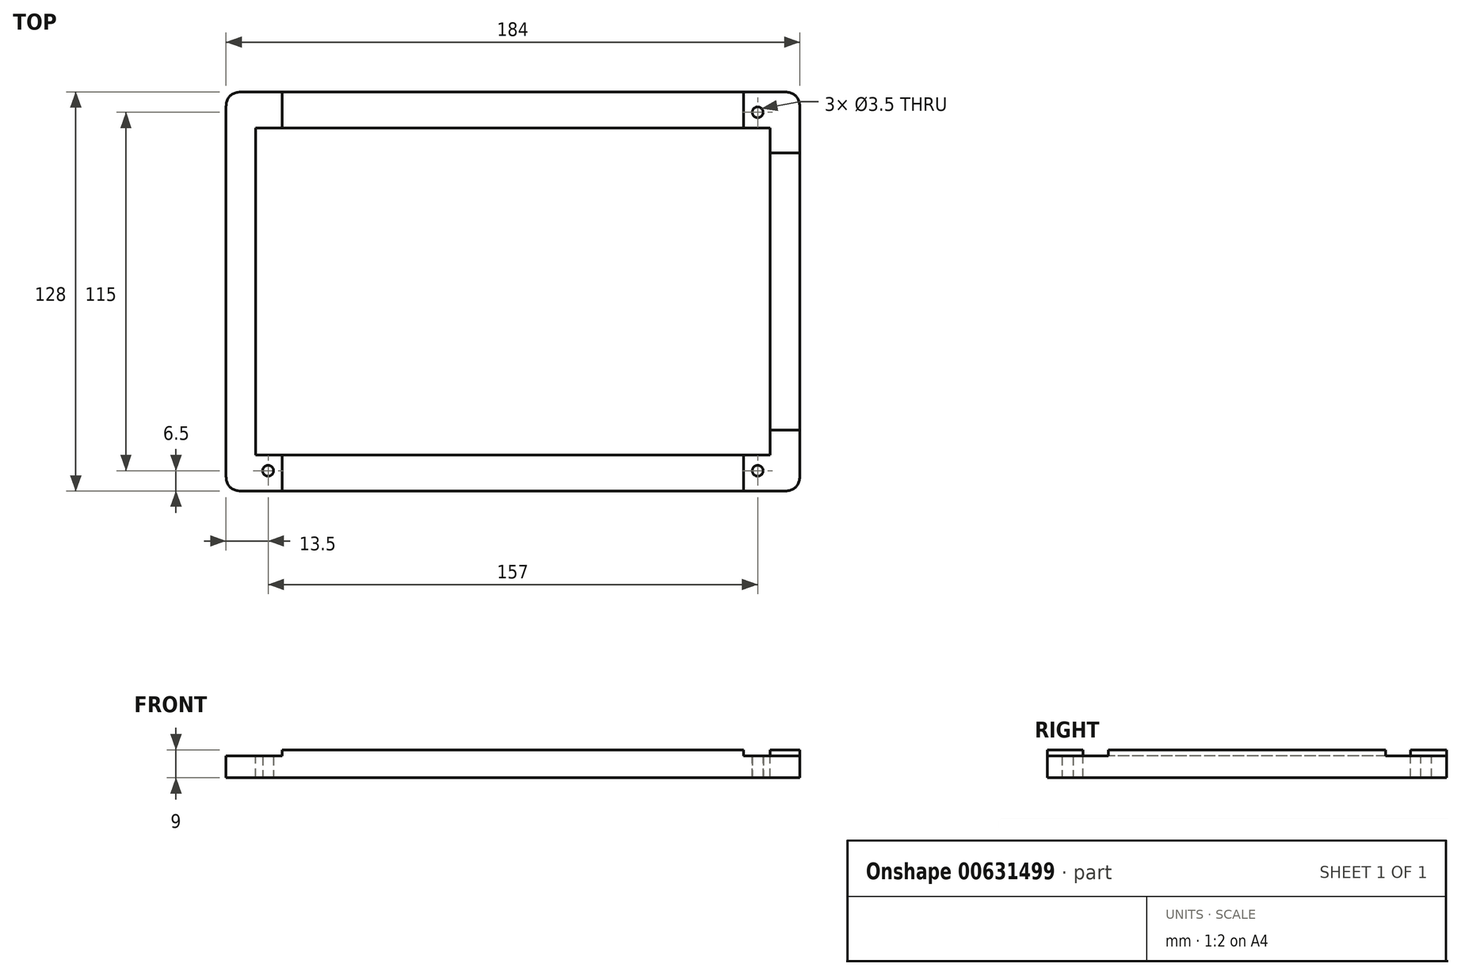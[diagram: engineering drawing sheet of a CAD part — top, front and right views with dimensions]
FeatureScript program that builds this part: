
annotation { "Feature Type Name" : "Feature", "Feature Type Description" : "" }
export const myFeature = defineFeature(function(context is Context, id is Id, definition is map)
    precondition{}
    {
        {
            var Q0;
            Q0=qCreatedBy(makeId("Top.planeOp"),FACE);
            var sketch = newSketch(context, id + "F0", { "sketchPlane" : qUnion([Q0])});
            skLineSegment(sketch, "E0.bottom", {"start": v(92, 64) * mm, "end": v(-92, 64) * mm});
            skLineSegment(sketch, "E0.top", {"start": v(92, -64) * mm, "end": v(-92, -64) * mm});
            skLineSegment(sketch, "E0.left", {"start": v(92, 64) * mm, "end": v(92, -64) * mm});
            skLineSegment(sketch, "E0.right", {"start": v(-92, 64) * mm, "end": v(-92, -64) * mm});
            skPoint(sketch, "E0.middle", {"position": v(0, 0) * mm});
            skSolve(sketch);
        }
        {
            var Q0;
            Q0=makeQuery(id+"F0.imprint","IMPRINT",FACE,{"disambiguationData":[TD([[makeQuery(id+"F0.imprint","IMPRINT",EDGE,{"derivedFrom":sQuery(id+"F0.wireOp",EDGE,"E0.bottom")}),1.0]])]});
            extrude(context, id + "F1", {"entities" : qUnion([Q0]), "depth" : 7 * mm, "offsetDistance" : 25.4 * mm});
        }
        {
            var Q0;
            Q0=makeQuery(id+"F1.opExtrude","CAP_FACE",FACE,{"disambiguationData":[OSD([sQuery(id+"F0.wireOp",EDGE,"E0.bottom"),sQuery(id+"F0.wireOp",EDGE,"E0.top"),sQuery(id+"F0.wireOp",EDGE,"E0.left"),sQuery(id+"F0.wireOp",EDGE,"E0.right")])],"isStart":false});
            var sketch = newSketch(context, id + "F2", { "sketchPlane" : qUnion([Q0])});
            skLineSegment(sketch, "E1.bottom", {"start": v(82.5, 52.5) * mm, "end": v(-82.5, 52.5) * mm});
            skLineSegment(sketch, "E1.top", {"start": v(82.5, -52.5) * mm, "end": v(-82.5, -52.5) * mm});
            skLineSegment(sketch, "E1.left", {"start": v(82.5, 52.5) * mm, "end": v(82.5, -52.5) * mm});
            skLineSegment(sketch, "E1.right", {"start": v(-82.5, 52.5) * mm, "end": v(-82.5, -52.5) * mm});
            skPoint(sketch, "E1.middle", {"position": v(0, 0) * mm});
            skSolve(sketch);
        }
        {
            var Q0;
            Q0=makeQuery(id+"F2.imprint","IMPRINT",FACE,{"disambiguationData":[TD([[makeQuery(id+"F2.imprint","IMPRINT",EDGE,{"derivedFrom":sQuery(id+"F2.wireOp",EDGE,"E1.bottom")}),1.0]])]});
            var Q1;
            Q1=makeQuery(id+"F1.opExtrude","CAP_FACE",FACE,{"disambiguationData":[OSD([sQuery(id+"F0.wireOp",EDGE,"E0.bottom"),sQuery(id+"F0.wireOp",EDGE,"E0.top"),sQuery(id+"F0.wireOp",EDGE,"E0.left"),sQuery(id+"F0.wireOp",EDGE,"E0.right")])],"isStart":true});
            extrude(context, id + "F3", {"entities" : qUnion([Q0]), "operationType" : NewBodyOperationType.REMOVE, "endBound" : BoundingType.UP_TO_SURFACE, "oppositeDirection" : true, "depth" : 25.4 * mm, "endBoundEntityFace" : qUnion([Q1]), "offsetDistance" : 25.4 * mm});
        }
        {
            var Q0;
            Q0=makeQuery(id+"F1.opExtrude","CAP_FACE",FACE,{"disambiguationData":[OSD([sQuery(id+"F0.wireOp",EDGE,"E0.bottom"),sQuery(id+"F0.wireOp",EDGE,"E0.top"),sQuery(id+"F0.wireOp",EDGE,"E0.left"),sQuery(id+"F0.wireOp",EDGE,"E0.right")])],"isStart":false});
            var sketch = newSketch(context, id + "F4", { "sketchPlane" : qUnion([Q0])});
            skLineSegment(sketch, "E2", {"start": v(0, 64) * mm, "end": v(0, 52.5) * mm});
            skLineSegment(sketch, "E3.bottom", {"start": v(74, 64) * mm, "end": v(-74, 64) * mm});
            skLineSegment(sketch, "E3.top", {"start": v(74, 52.5) * mm, "end": v(-74, 52.5) * mm});
            skLineSegment(sketch, "E3.left", {"start": v(74, 64) * mm, "end": v(74, 52.5) * mm});
            skLineSegment(sketch, "E3.right", {"start": v(-74, 64) * mm, "end": v(-74, 52.5) * mm});
            skPoint(sketch, "E3.middle", {"position": v(0, 58.25) * mm});
            skLineSegment(sketch, "E4", {"start": v(0, -52.5) * mm, "end": v(0, -64) * mm});
            skLineSegment(sketch, "E5.bottom", {"start": v(74, -52.5) * mm, "end": v(-74, -52.5) * mm});
            skLineSegment(sketch, "E5.top", {"start": v(74, -64) * mm, "end": v(-74, -64) * mm});
            skLineSegment(sketch, "E5.left", {"start": v(74, -52.5) * mm, "end": v(74, -64) * mm});
            skLineSegment(sketch, "E5.right", {"start": v(-74, -52.5) * mm, "end": v(-74, -64) * mm});
            skPoint(sketch, "E5.middle", {"position": v(0, -58.25) * mm});
            skSolve(sketch);
        }
        {
            var Q0;
            {var subQ0=sQuery(id+"F4.wireOp",EDGE,"E2");Q0=makeQuery(id+"F4.imprint","IMPRINT",FACE,{"disambiguationData":[TD([[makeQuery(id+"F4.imprint","IMPRINT",EDGE,{"derivedFrom":subQ0}),-1.0]])]});}
            var Q1;
            {var subQ0=sQuery(id+"F4.wireOp",EDGE,"E2");Q1=makeQuery(id+"F4.imprint","IMPRINT",FACE,{"disambiguationData":[TD([[makeQuery(id+"F4.imprint","IMPRINT",EDGE,{"derivedFrom":subQ0}),1.0]])]});}
            var Q2;
            {var subQ0=sQuery(id+"F4.wireOp",EDGE,"E4");Q2=makeQuery(id+"F4.imprint","IMPRINT",FACE,{"disambiguationData":[TD([[makeQuery(id+"F4.imprint","IMPRINT",EDGE,{"derivedFrom":subQ0}),-1.0]])]});}
            var Q3;
            {var subQ0=sQuery(id+"F4.wireOp",EDGE,"E4");Q3=makeQuery(id+"F4.imprint","IMPRINT",FACE,{"disambiguationData":[TD([[makeQuery(id+"F4.imprint","IMPRINT",EDGE,{"derivedFrom":subQ0}),1.0]])]});}
            extrude(context, id + "F5", {"entities" : qUnion([Q0, Q1, Q2, Q3]), "operationType" : NewBodyOperationType.ADD, "depth" : 2 * mm, "offsetDistance" : 25.4 * mm});
        }
        {
            var Q0;
            Q0=makeQuery(id+"F1.opExtrude","SWEPT_EDGE",EDGE,{"disambiguationData":[OSD([sQuery(id+"F0.wireOp",EDGE,"E0.top"),sQuery(id+"F0.wireOp",EDGE,"E0.left")])]});
            var Q1;
            Q1=makeQuery(id+"F1.opExtrude","SWEPT_EDGE",EDGE,{"disambiguationData":[OSD([sQuery(id+"F0.wireOp",EDGE,"E0.bottom"),sQuery(id+"F0.wireOp",EDGE,"E0.left")])]});
            var Q2;
            Q2=makeQuery(id+"F1.opExtrude","SWEPT_EDGE",EDGE,{"disambiguationData":[OSD([sQuery(id+"F0.wireOp",EDGE,"E0.bottom"),sQuery(id+"F0.wireOp",EDGE,"E0.right")])]});
            var Q3;
            Q3=makeQuery(id+"F1.opExtrude","SWEPT_EDGE",EDGE,{"disambiguationData":[OSD([sQuery(id+"F0.wireOp",EDGE,"E0.top"),sQuery(id+"F0.wireOp",EDGE,"E0.right")])]});
            fillet(context, id + "F6", {"entities" : qUnion([Q0, Q1, Q2, Q3]), "radius" : 5.08 * mm, "tangentPropagation" : true, "rho" : 0.5, "crossSection" : FilletCrossSection.CONIC, "allowEdgeOverflow" : false});
        }
        {
            var Q0;
            {var subQ0=sQuery(id+"F0.wireOp",EDGE,"E0.bottom");var subQ1=sQuery(id+"F0.wireOp",EDGE,"E0.top");var subQ2=sQuery(id+"F0.wireOp",EDGE,"E0.left");Q0=makeQuery(id+"F5.boolean.opBoolean","SPLIT",FACE,{"disambiguationData":[TD([makeQuery(id+"F1.opExtrude","SWEPT_FACE",FACE,{"disambiguationData":[OSD([subQ2])]})])],"derivedFrom":makeQuery(id+"F1.opExtrude","CAP_FACE",FACE,{"disambiguationData":[OSD([subQ0,subQ1,subQ2,sQuery(id+"F0.wireOp",EDGE,"E0.right")])],"isStart":false})});}
            var sketch = newSketch(context, id + "F7", { "sketchPlane" : qUnion([Q0])});
            skLineSegment(sketch, "E6", {"start": v(92, 0) * mm, "end": v(82.5, 0) * mm});
            skLineSegment(sketch, "E7.bottom", {"start": v(92, -44.45) * mm, "end": v(82.5, -44.45) * mm});
            skLineSegment(sketch, "E7.top", {"start": v(92, 44.45) * mm, "end": v(82.5, 44.45) * mm});
            skLineSegment(sketch, "E7.left", {"start": v(92, -44.45) * mm, "end": v(92, 44.45) * mm});
            skLineSegment(sketch, "E7.right", {"start": v(82.5, -44.45) * mm, "end": v(82.5, 44.45) * mm});
            skPoint(sketch, "E7.middle", {"position": v(87.25, 0) * mm});
            skSolve(sketch);
        }
        {
            var Q0;
            {var subQ0=sQuery(id+"F7.wireOp",EDGE,"E6");Q0=makeQuery(id+"F7.imprint","IMPRINT",FACE,{"disambiguationData":[TD([[makeQuery(id+"F7.imprint","IMPRINT",EDGE,{"derivedFrom":subQ0}),1.0]])]});}
            var Q1;
            {var subQ0=sQuery(id+"F7.wireOp",EDGE,"E6");Q1=makeQuery(id+"F7.imprint","IMPRINT",FACE,{"disambiguationData":[TD([[makeQuery(id+"F7.imprint","IMPRINT",EDGE,{"derivedFrom":subQ0}),-1.0]])]});}
            extrude(context, id + "F8", {"entities" : qUnion([Q0, Q1]), "operationType" : NewBodyOperationType.ADD, "depth" : 2 * mm, "offsetDistance" : 25.4 * mm});
        }
        {
            var Q0;
            {var subQ1=sQuery(id+"F0.wireOp",EDGE,"E0.left");var subQ2=sQuery(id+"F0.wireOp",EDGE,"E0.bottom");var subQ5=makeQuery(id+"F1.opExtrude","SWEPT_FACE",FACE,{"disambiguationData":[OSD([subQ2])]});var subQ6=makeQuery(id+"F1.opExtrude","SWEPT_FACE",FACE,{"disambiguationData":[OSD([subQ1])]});var subQ9=sQuery(id+"F0.wireOp",EDGE,"E0.top");Q0=makeQuery(id+"F8.boolean.opBoolean","SPLIT",FACE,{"disambiguationData":[TD([subQ5])],"derivedFrom":makeQuery(id+"F5.boolean.opBoolean","SPLIT",FACE,{"disambiguationData":[TD([subQ6])],"derivedFrom":makeQuery(id+"F1.opExtrude","CAP_FACE",FACE,{"disambiguationData":[OSD([subQ2,subQ9,subQ1,sQuery(id+"F0.wireOp",EDGE,"E0.right")])],"isStart":false})})});}
            var sketch = newSketch(context, id + "F9", { "sketchPlane" : qUnion([Q0])});
            skLineSegment(sketch, "E8", {"start": v(82.5, 49.76) * mm, "end": v(78.5, 49.76) * mm});
            skLineSegment(sketch, "E9", {"start": v(78.5, 49.76) * mm, "end": v(78.5, 57.5) * mm});
            skCircle(sketch, "E10", {"center": v(78.5, 57.5) * mm, "radius": 1.75 * mm});
            skSolve(sketch);
        }
        {
            var Q0;
            Q0=makeQuery(id+"F9.imprint","IMPRINT",FACE,{"disambiguationData":[TD([[makeQuery(id+"F9.imprint","IMPRINT",EDGE,{"derivedFrom":sQuery(id+"F9.wireOp",EDGE,"E10")}),1.0]])]});
            var Q1;
            Q1=makeQuery(id+"F1.opExtrude","CAP_FACE",FACE,{"disambiguationData":[OSD([sQuery(id+"F0.wireOp",EDGE,"E0.bottom"),sQuery(id+"F0.wireOp",EDGE,"E0.top"),sQuery(id+"F0.wireOp",EDGE,"E0.left"),sQuery(id+"F0.wireOp",EDGE,"E0.right")])],"isStart":true});
            extrude(context, id + "F10", {"entities" : qUnion([Q0]), "operationType" : NewBodyOperationType.REMOVE, "endBound" : BoundingType.UP_TO_SURFACE, "oppositeDirection" : true, "depth" : 25.4 * mm, "endBoundEntityFace" : qUnion([Q1]), "offsetDistance" : 25.4 * mm});
        }
        {
            var Q0;
            Q0=makeQuery(id+"F1.opExtrude","CAP_FACE",FACE,{"disambiguationData":[OSD([sQuery(id+"F0.wireOp",EDGE,"E0.bottom"),sQuery(id+"F0.wireOp",EDGE,"E0.top"),sQuery(id+"F0.wireOp",EDGE,"E0.left"),sQuery(id+"F0.wireOp",EDGE,"E0.right")])],"isStart":true});
            var sketch = newSketch(context, id + "F11", { "sketchPlane" : qUnion([Q0])});
            skLineSegment(sketch, "E11", {"start": v(78.5, -57.5) * mm, "end": v(78.5, 57.5) * mm});
            skLineSegment(sketch, "E12", {"start": v(-78.5, -57.5) * mm, "end": v(-78.5, 57.5) * mm});
            skCircle(sketch, "E13", {"center": v(-78.5, 57.5) * mm, "radius": 1.75 * mm});
            skCircle(sketch, "E14", {"center": v(78.5, 57.5) * mm, "radius": 1.75 * mm});
            skSolve(sketch);
        }
        {
            var Q0;
            Q0=makeQuery(id+"F11.imprint","IMPRINT",FACE,{"disambiguationData":[TD([[makeQuery(id+"F11.imprint","IMPRINT",EDGE,{"derivedFrom":sQuery(id+"F11.wireOp",EDGE,"E13")}),1.0]])]});
            var Q1;
            Q1=makeQuery(id+"F11.imprint","IMPRINT",FACE,{"disambiguationData":[TD([[makeQuery(id+"F11.imprint","IMPRINT",EDGE,{"derivedFrom":sQuery(id+"F11.wireOp",EDGE,"E14")}),1.0]])]});
            var Q2;
            {var subQ1=sQuery(id+"F0.wireOp",EDGE,"E0.top");var subQ2=makeQuery(id+"F1.opExtrude","SWEPT_FACE",FACE,{"disambiguationData":[OSD([subQ1])]});var subQ4=sQuery(id+"F0.wireOp",EDGE,"E0.right");var subQ5=makeQuery(id+"F1.opExtrude","SWEPT_FACE",FACE,{"disambiguationData":[OSD([subQ4])]});var subQ9=sQuery(id+"F0.wireOp",EDGE,"E0.bottom");Q2=makeQuery(id+"F1bPiPXSSVC8fBb_1.1.F8.boolean.opBoolean","SPLIT",FACE,{"disambiguationData":[TD([subQ2])],"derivedFrom":makeQuery(id+"F5.boolean.opBoolean","SPLIT",FACE,{"disambiguationData":[TD([subQ5])],"derivedFrom":makeQuery(id+"F1.opExtrude","CAP_FACE",FACE,{"disambiguationData":[OSD([subQ9,subQ1,sQuery(id+"F0.wireOp",EDGE,"E0.left"),subQ4])],"isStart":false})})});}
            extrude(context, id + "F12", {"entities" : qUnion([Q0, Q1]), "operationType" : NewBodyOperationType.REMOVE, "endBound" : BoundingType.UP_TO_SURFACE, "oppositeDirection" : true, "depth" : 25.4 * mm, "endBoundEntityFace" : qUnion([Q2]), "offsetDistance" : 25.4 * mm});
        }
    });
